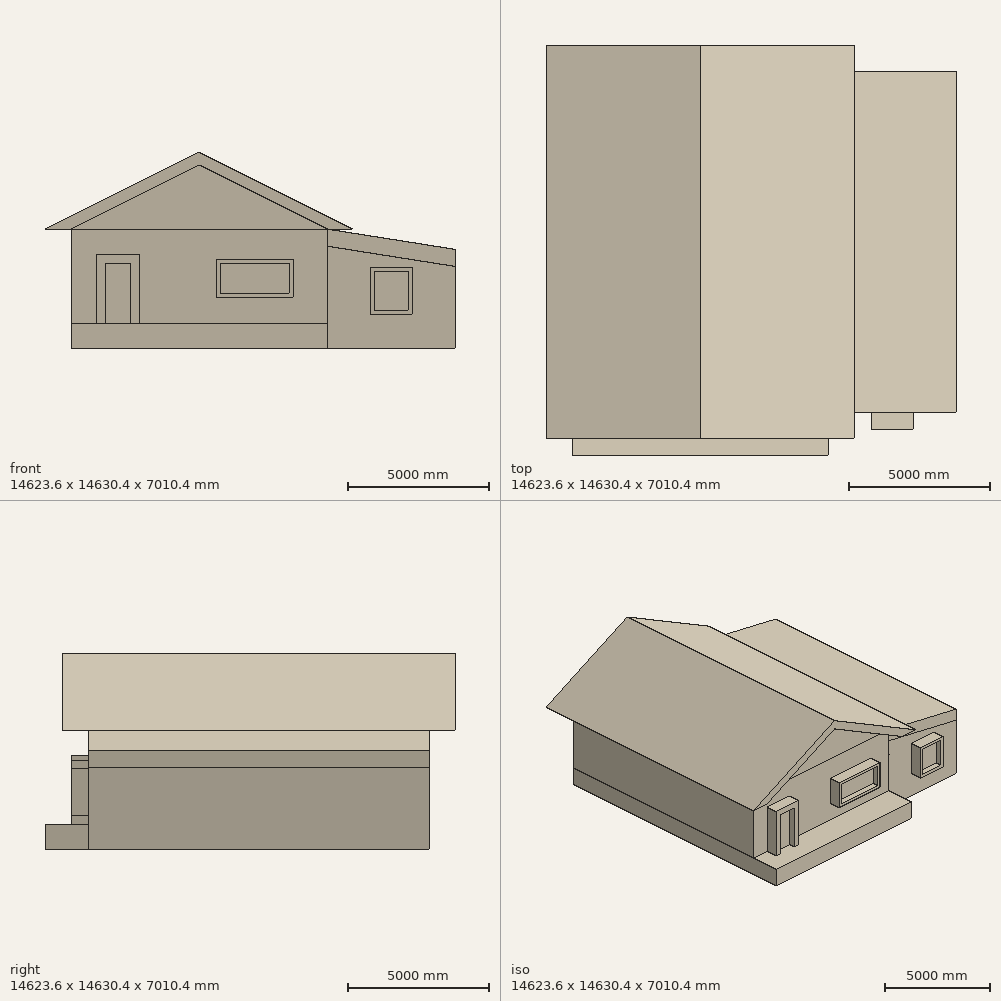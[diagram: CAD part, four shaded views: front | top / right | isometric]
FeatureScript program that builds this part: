
annotation { "Feature Type Name" : "Feature", "Feature Type Description" : "" }
export const myFeature = defineFeature(function(context is Context, id is Id, definition is map)
    precondition{}
    {
        {
            var Q0;
            Q0=qCreatedBy(makeId("Front.planeOp"),FACE);
            var sketch = newSketch(context, id + "F0", { "sketchPlane" : qUnion([Q0])});
            skLineSegment(sketch, "E0", {"start": v(0, 0) * mm, "end": v(-4572, 0) * mm});
            skLineSegment(sketch, "E1", {"start": v(0, 0) * mm, "end": v(4572, 0) * mm});
            skLineSegment(sketch, "E2.bottom", {"start": v(-4572, 0) * mm, "end": v(4572, 0) * mm});
            skLineSegment(sketch, "E2.top", {"start": v(-4572, -3352.8) * mm, "end": v(4572, -3352.8) * mm});
            skLineSegment(sketch, "E2.left", {"start": v(-4572, 0) * mm, "end": v(-4572, -3352.8) * mm});
            skLineSegment(sketch, "E2.right", {"start": v(4572, 0) * mm, "end": v(4572, -3352.8) * mm});
            skLineSegment(sketch, "E3", {"start": v(0, 0) * mm, "end": v(0, 2286) * mm});
            skLineSegment(sketch, "E4", {"start": v(0, 2286) * mm, "end": v(4572, 0) * mm});
            skLineSegment(sketch, "E5", {"start": v(0, 2286) * mm, "end": v(-4572, 0) * mm});
            skLineSegment(sketch, "E6", {"start": v(-4572, 0) * mm, "end": v(-5486.4, 0) * mm});
            skLineSegment(sketch, "E7", {"start": v(-5486.4, 0) * mm, "end": v(0, 2743.2) * mm});
            skLineSegment(sketch, "E8", {"start": v(0, 2743.2) * mm, "end": v(0, 2286) * mm});
            skLineSegment(sketch, "E9", {"start": v(0, 2743.2) * mm, "end": v(5486.4, 0) * mm});
            skLineSegment(sketch, "E10", {"start": v(5486.4, 0) * mm, "end": v(4572, 0) * mm});
            skLineSegment(sketch, "E11", {"start": v(-4572, -3352.8) * mm, "end": v(-4572, -4267.2) * mm});
            skLineSegment(sketch, "E12", {"start": v(4572, -3352.8) * mm, "end": v(4572, -4267.2) * mm});
            skLineSegment(sketch, "E13", {"start": v(4572, -4267.2) * mm, "end": v(-4572, -4267.2) * mm});
            skLineSegment(sketch, "E14", {"start": v(4572, 0) * mm, "end": v(9126.85, -721.42) * mm});
            skLineSegment(sketch, "E15", {"start": v(9126.85, -721.42) * mm, "end": v(9126.85, -1331.02) * mm});
            skLineSegment(sketch, "E16", {"start": v(9126.85, -1331.02) * mm, "end": v(4572, -609.6) * mm});
            skLineSegment(sketch, "E17", {"start": v(4572, -4267.2) * mm, "end": v(9137.25, -4267.2) * mm});
            skLineSegment(sketch, "E18", {"start": v(9137.25, -4267.2) * mm, "end": v(9126.85, -1331.02) * mm});
            skLineSegment(sketch, "E19", {"start": v(4572, -3352.8) * mm, "end": v(9126.85, -3352.8) * mm});
            skLineSegment(sketch, "E20.0", {"start": v(4571.22, -4.94) * mm, "end": v(9126.07, -726.36) * mm});
            skLineSegment(sketch, "E21", {"start": v(-3352.8, -3352.8) * mm, "end": v(-3352.8, -1219.2) * mm});
            skLineSegment(sketch, "E22", {"start": v(-3352.8, -1219.2) * mm, "end": v(-2438.4, -1219.2) * mm});
            skLineSegment(sketch, "E23", {"start": v(-2438.4, -1219.2) * mm, "end": v(-2438.4, -3352.8) * mm});
            skLineSegment(sketch, "E24.0", {"start": v(-2133.6, -914.4) * mm, "end": v(-2133.6, -3352.8) * mm});
            skLineSegment(sketch, "E24.1", {"start": v(-3657.6, -914.4) * mm, "end": v(-2133.6, -914.4) * mm});
            skLineSegment(sketch, "E24.2", {"start": v(-3657.6, -3352.8) * mm, "end": v(-3657.6, -914.4) * mm});
            skLineSegment(sketch, "E25", {"start": v(609.6, -1066.8) * mm, "end": v(609.6, -2438.4) * mm});
            skLineSegment(sketch, "E26", {"start": v(609.6, -2438.4) * mm, "end": v(3352.8, -2438.4) * mm});
            skLineSegment(sketch, "E27", {"start": v(3352.8, -2438.4) * mm, "end": v(3352.8, -1066.8) * mm});
            skLineSegment(sketch, "E28", {"start": v(609.6, -1066.8) * mm, "end": v(3352.8, -1066.8) * mm});
            skLineSegment(sketch, "E29.0", {"start": v(762, -1219.2) * mm, "end": v(3200.4, -1219.2) * mm});
            skLineSegment(sketch, "E29.1", {"start": v(762, -1219.2) * mm, "end": v(762, -2286) * mm});
            skLineSegment(sketch, "E29.2", {"start": v(762, -2286) * mm, "end": v(3200.4, -2286) * mm});
            skLineSegment(sketch, "E29.3", {"start": v(3200.4, -2286) * mm, "end": v(3200.4, -1219.2) * mm});
            skLineSegment(sketch, "E30", {"start": v(6248.4, -1524) * mm, "end": v(6248.4, -2895.6) * mm});
            skLineSegment(sketch, "E31", {"start": v(6248.4, -2895.6) * mm, "end": v(7467.6, -2895.6) * mm});
            skLineSegment(sketch, "E32", {"start": v(7467.6, -2895.6) * mm, "end": v(7467.6, -1524) * mm});
            skLineSegment(sketch, "E33", {"start": v(7467.6, -1524) * mm, "end": v(6248.4, -1524) * mm});
            skLineSegment(sketch, "E34.0", {"start": v(7620, -1371.6) * mm, "end": v(6096, -1371.6) * mm});
            skLineSegment(sketch, "E34.1", {"start": v(7620, -3048) * mm, "end": v(7620, -1371.6) * mm});
            skLineSegment(sketch, "E34.2", {"start": v(6096, -3048) * mm, "end": v(7620, -3048) * mm});
            skLineSegment(sketch, "E34.3", {"start": v(6096, -1371.6) * mm, "end": v(6096, -3048) * mm});
            skSolve(sketch);
        }
        {
            var Q0;
            Q0=makeQuery(id+"F0.imprint","IMPRINT",FACE,{"disambiguationData":[TD([[makeQuery(id+"F0.imprint","IMPRINT",EDGE,{"derivedFrom":sQuery(id+"F0.wireOp",EDGE,"E5")}),-1.0]])]});
            var Q1;
            Q1=makeQuery(id+"F0.imprint","IMPRINT",FACE,{"disambiguationData":[TD([[makeQuery(id+"F0.imprint","IMPRINT",EDGE,{"derivedFrom":sQuery(id+"F0.wireOp",EDGE,"E4")}),1.0]])]});
            extrude(context, id + "F1", {"entities" : qUnion([Q0, Q1]), "depth" : 13106.4 * mm, "offsetDistance" : 30.48 * mm, "hasSecondDirection" : true, "secondDirectionOppositeDirection" : true, "secondDirectionDepth" : 914.4 * mm});
        }
        {
            var Q0;
            {var subQ2=sQuery(id+"F0.wireOp",EDGE,"E3");Q0=makeQuery(id+"F0.imprint","IMPRINT",FACE,{"disambiguationData":[TD([[makeQuery(id+"F0.imprint","IMPRINT",EDGE,{"derivedFrom":subQ2}),1.0]])]});}
            var Q1;
            {var subQ2=sQuery(id+"F0.wireOp",EDGE,"E3");Q1=makeQuery(id+"F0.imprint","IMPRINT",FACE,{"disambiguationData":[TD([[makeQuery(id+"F0.imprint","IMPRINT",EDGE,{"derivedFrom":subQ2}),-1.0]])]});}
            extrude(context, id + "F2", {"entities" : qUnion([Q0, Q1]), "operationType" : NewBodyOperationType.ADD, "depth" : 12192 * mm, "offsetDistance" : 30.48 * mm, "hasSecondDirection" : true, "secondDirectionOppositeDirection" : true, "secondDirectionDepth" : 30.48 * mm});
        }
        {
            var Q0;
            {var subQ0=sQuery(id+"F0.wireOp",EDGE,"E14");Q0=makeQuery(id+"F0.imprint","IMPRINT",FACE,{"disambiguationData":[TD([[makeQuery(id+"F0.imprint","IMPRINT",EDGE,{"derivedFrom":subQ0}),-1.0]])]});}
            extrude(context, id + "F3", {"entities" : qUnion([Q0]), "depth" : 12192 * mm, "offsetDistance" : 30.48 * mm});
        }
        {
            var Q0;
            {var subQ5=sQuery(id+"F0.wireOp",EDGE,"E11");Q0=makeQuery(id+"F0.imprint","IMPRINT",FACE,{"disambiguationData":[TD([[makeQuery(id+"F0.imprint","IMPRINT",EDGE,{"derivedFrom":subQ5}),1.0]])]});}
            extrude(context, id + "F4", {"entities" : qUnion([Q0]), "depth" : 13716 * mm, "offsetDistance" : 30.48 * mm});
        }
        {
            var Q0;
            {var subQ9=sQuery(id+"F0.wireOp",EDGE,"E2.left");Q0=makeQuery(id+"F0.imprint","IMPRINT",FACE,{"disambiguationData":[TD([[makeQuery(id+"F0.imprint","IMPRINT",EDGE,{"derivedFrom":subQ9}),1.0]])]});}
            extrude(context, id + "F5", {"entities" : qUnion([Q0]), "depth" : 12192 * mm, "offsetDistance" : 30.48 * mm});
        }
        {
            var Q0;
            {var subQ0=sQuery(id+"F0.wireOp",EDGE,"E21");Q0=makeQuery(id+"F0.imprint","IMPRINT",FACE,{"disambiguationData":[TD([[makeQuery(id+"F0.imprint","IMPRINT",EDGE,{"derivedFrom":subQ0}),-1.0]])]});}
            extrude(context, id + "F6", {"entities" : qUnion([Q0]), "operationType" : NewBodyOperationType.ADD, "depth" : 12496.8 * mm, "offsetDistance" : 30.48 * mm});
        }
        {
            var Q0;
            {var subQ0=sQuery(id+"F0.wireOp",EDGE,"E21");Q0=makeQuery(id+"F0.imprint","IMPRINT",FACE,{"disambiguationData":[TD([[makeQuery(id+"F0.imprint","IMPRINT",EDGE,{"derivedFrom":subQ0}),1.0]])]});}
            extrude(context, id + "F7", {"entities" : qUnion([Q0]), "depth" : 12801.6 * mm, "offsetDistance" : 30.48 * mm});
        }
        {
            var Q0;
            Q0=makeQuery(id+"F0.imprint","IMPRINT",FACE,{"disambiguationData":[TD([[makeQuery(id+"F0.imprint","IMPRINT",EDGE,{"derivedFrom":sQuery(id+"F0.wireOp",EDGE,"E29.0")}),-1.0]])]});
            extrude(context, id + "F8", {"entities" : qUnion([Q0]), "depth" : 12496.8 * mm, "offsetDistance" : 30.48 * mm});
        }
        {
            var Q0;
            Q0=makeQuery(id+"F0.imprint","IMPRINT",FACE,{"disambiguationData":[TD([[makeQuery(id+"F0.imprint","IMPRINT",EDGE,{"derivedFrom":sQuery(id+"F0.wireOp",EDGE,"E25")}),1.0]])]});
            extrude(context, id + "F9", {"entities" : qUnion([Q0]), "depth" : 12801.6 * mm, "offsetDistance" : 30.48 * mm});
        }
        {
            var Q0;
            {var subQ1=sQuery(id+"F0.wireOp",EDGE,"E12");Q0=makeQuery(id+"F0.imprint","IMPRINT",FACE,{"disambiguationData":[TD([[makeQuery(id+"F0.imprint","IMPRINT",EDGE,{"derivedFrom":subQ1}),1.0]])]});}
            extrude(context, id + "F10", {"entities" : qUnion([Q0]), "depth" : 12192 * mm, "offsetDistance" : 30.48 * mm});
        }
        {
            var Q0;
            Q0=makeQuery(id+"F0.imprint","IMPRINT",FACE,{"disambiguationData":[TD([[makeQuery(id+"F0.imprint","IMPRINT",EDGE,{"derivedFrom":sQuery(id+"F0.wireOp",EDGE,"E30")}),1.0]])]});
            extrude(context, id + "F11", {"entities" : qUnion([Q0]), "depth" : 12496.8 * mm, "offsetDistance" : 30.48 * mm});
        }
        {
            var Q0;
            Q0=makeQuery(id+"F0.imprint","IMPRINT",FACE,{"disambiguationData":[TD([[makeQuery(id+"F0.imprint","IMPRINT",EDGE,{"derivedFrom":sQuery(id+"F0.wireOp",EDGE,"E30")}),-1.0]])]});
            extrude(context, id + "F12", {"entities" : qUnion([Q0]), "depth" : 12801.6 * mm, "offsetDistance" : 30.48 * mm});
        }
    });
